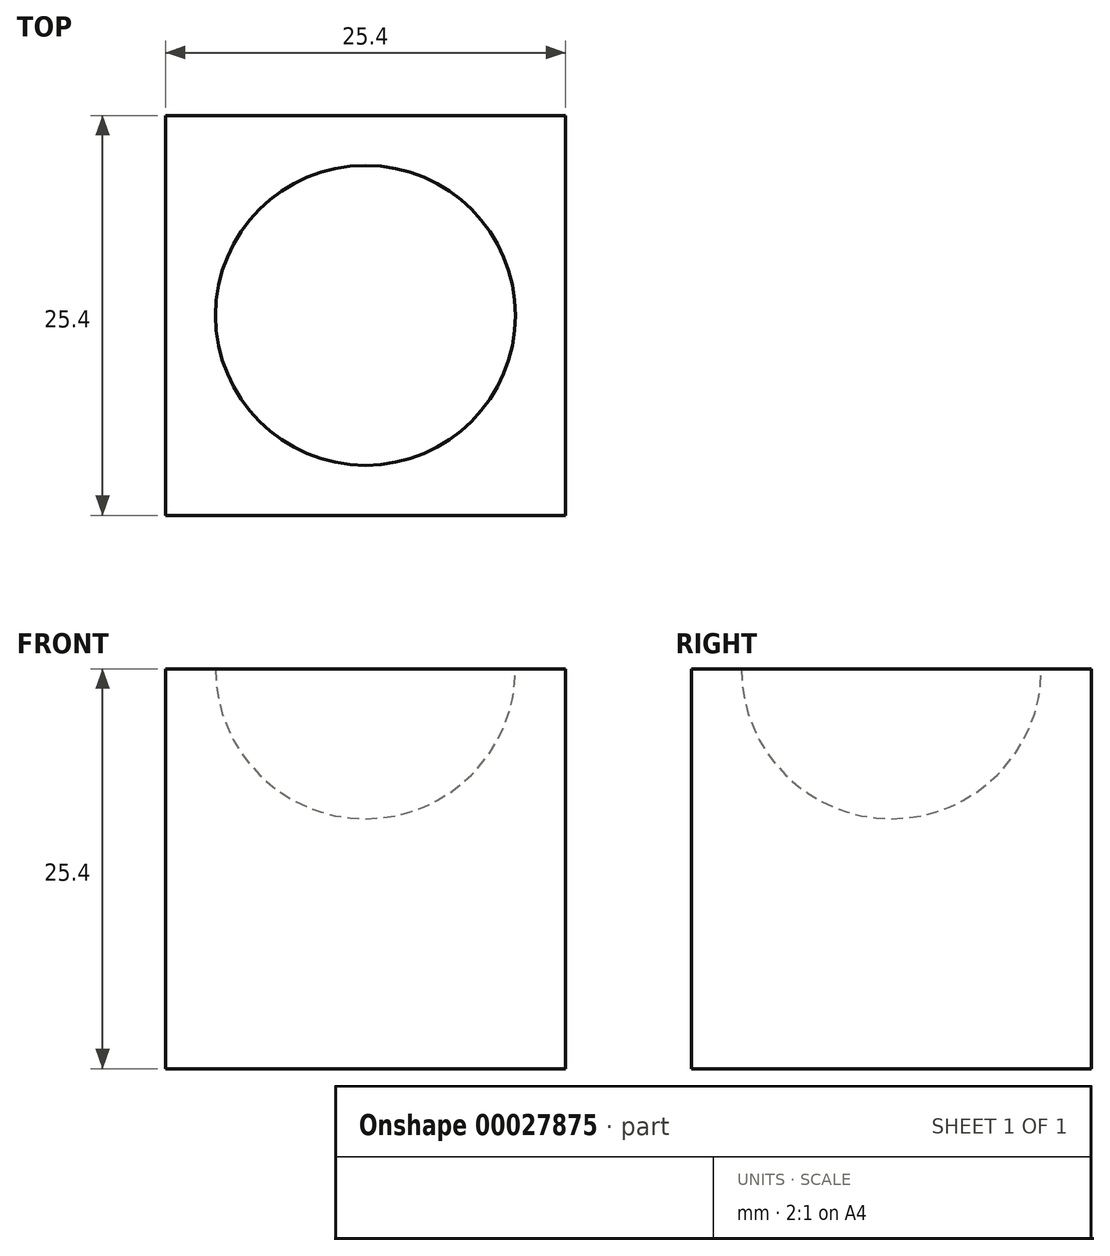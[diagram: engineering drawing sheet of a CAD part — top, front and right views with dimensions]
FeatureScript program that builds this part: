
annotation { "Feature Type Name" : "Feature", "Feature Type Description" : "" }
export const myFeature = defineFeature(function(context is Context, id is Id, definition is map)
    precondition{}
    {
        {
            var Q0;
            Q0=qCreatedBy(makeId("Front.planeOp"),FACE);
            var sketch = newSketch(context, id + "F0", { "sketchPlane" : qUnion([Q0])});
            skLineSegment(sketch, "E0.bottom", {"start": v(-10.04, 0) * mm, "end": v(15.36, 0) * mm});
            skLineSegment(sketch, "E0.top", {"start": v(-10.04, -25.4) * mm, "end": v(15.36, -25.4) * mm});
            skLineSegment(sketch, "E0.left", {"start": v(-10.04, 0) * mm, "end": v(-10.04, -25.4) * mm});
            skLineSegment(sketch, "E0.right", {"start": v(15.36, 0) * mm, "end": v(15.36, -25.4) * mm});
            skSolve(sketch);
        }
        {
            var Q0;
            Q0 = qSketchRegion(id + "F0", true);
            extrude(context, id + "F1", {"entities" : qUnion([Q0]), "depth" : 25.4 * mm});
        }
        {
            var Q0;
            Q0=makeQuery(id+"F1.opExtrude","SWEPT_FACE",FACE,{"disambiguationData":[OSD([sQuery(id+"F0.wireOp",EDGE,"E0.bottom")])]});
            var sketch = newSketch(context, id + "F2", { "sketchPlane" : qUnion([Q0])});
            skLineSegment(sketch, "E1", {"start": v(-10.04, -12.7) * mm, "end": v(15.36, -12.7) * mm});
            skLineSegment(sketch, "E2", {"start": v(2.66, 0) * mm, "end": v(2.66, -25.4) * mm});
            skCircle(sketch, "E3", {"center": v(2.66, -12.7) * mm, "radius": 9.53 * mm});
            skSolve(sketch);
        }
        {
            var Q0;
            {var subQ1=sQuery(id+"F2.wireOp",EDGE,"E2");var subQ3=sQuery(id+"F2.wireOp",EDGE,"E1");var subQ5=makeQuery(id+"F2.imprint","INTERSECT",VERTEX,{"derivedFrom":[subQ3,subQ1]});Q0=makeQuery(id+"F2.imprint","IMPRINT",FACE,{"disambiguationData":[TD([[makeQuery(id+"F2.imprint","IMPRINT",EDGE,{"disambiguationData":[TD([[subQ5,-1.0]])],"derivedFrom":subQ3}),1.0]])]});}
            var Q1;
            {var subQ0=sQuery(id+"F2.wireOp",EDGE,"E3");var subQ3=sQuery(id+"F2.wireOp",EDGE,"E1");var subQ4=makeQuery(id+"F2.imprint","INTERSECT",VERTEX,{"disambiguationData":[OD(0.0)],"derivedFrom":[subQ3,subQ0]});Q1=makeQuery(id+"F2.imprint","IMPRINT",FACE,{"disambiguationData":[TD([[makeQuery(id+"F2.imprint","IMPRINT",EDGE,{"disambiguationData":[TD([[subQ4,-1.0]])],"derivedFrom":subQ3}),1.0]])]});}
            var Q2;
            Q2=sQuery(id+"F2.wireOp",EDGE,"E1");
            revolve(context, id + "F3", {"operationType" : NewBodyOperationType.REMOVE, "entities" : qUnion([Q0, Q1]), "axis" : qUnion([Q2]), "revolveType" : RevolveType.FULL, "oppositeDirection" : true});
        }
    });
